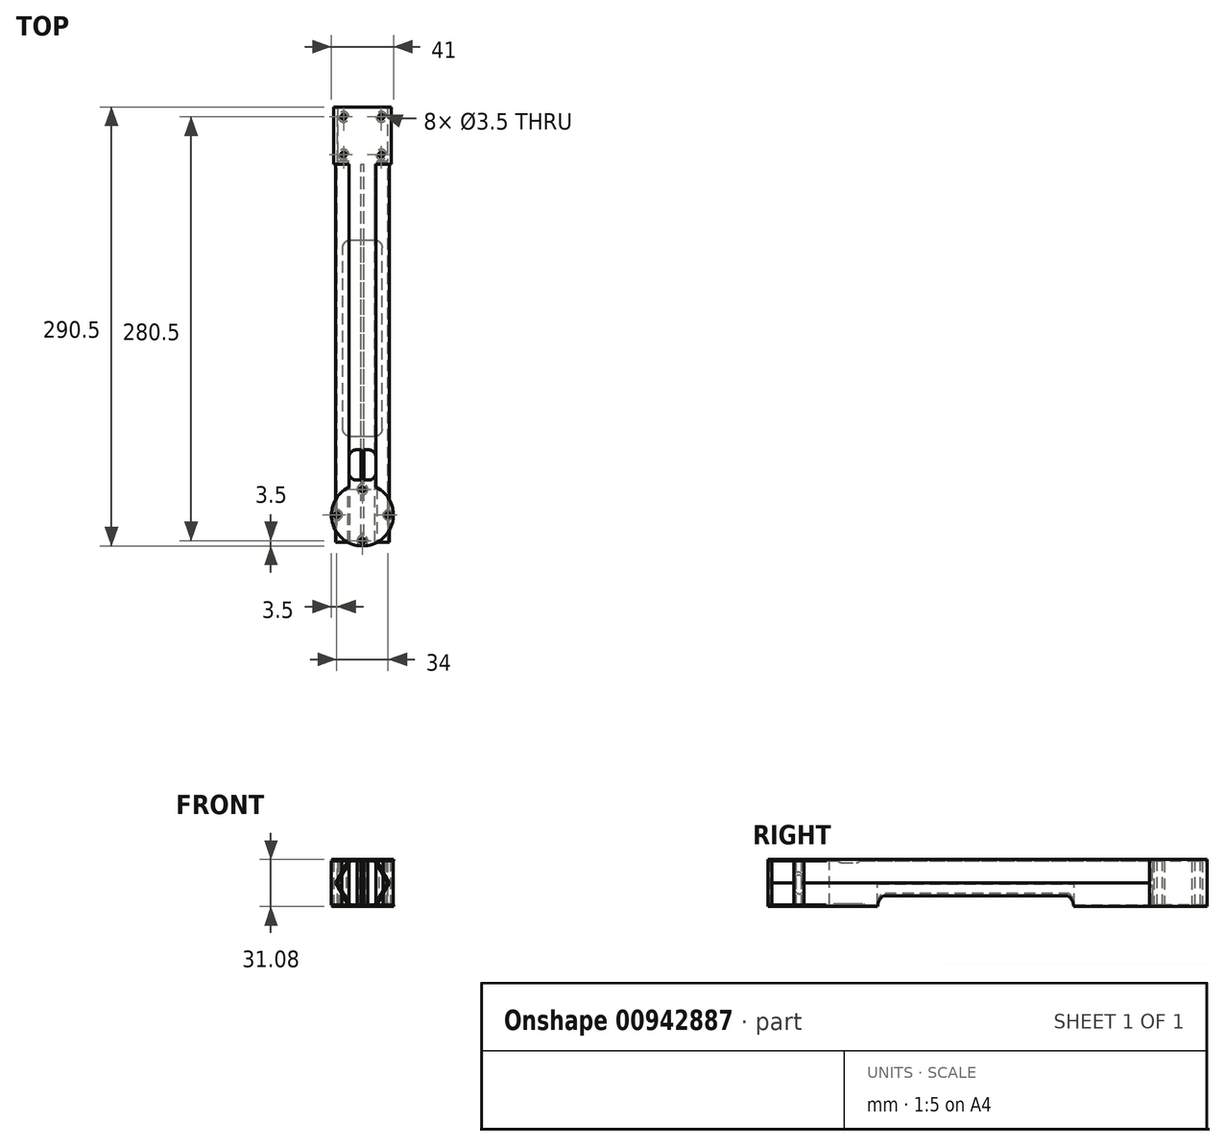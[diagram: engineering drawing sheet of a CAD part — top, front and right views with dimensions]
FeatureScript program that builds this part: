
annotation { "Feature Type Name" : "Feature", "Feature Type Description" : "" }
export const myFeature = defineFeature(function(context is Context, id is Id, definition is map)
    precondition{}
    {
        {
            var Q0;
            Q0=qCreatedBy(makeId("Front.planeOp"),FACE);
            var sketch = newSketch(context, id + "F0", { "sketchPlane" : qUnion([Q0])});
            skCircle(sketch, "E0.cCircle", {"center": v(0, 0) * mm, "radius": 14.5 * mm, "construction": true});
            skLineSegment(sketch, "E0.0", {"start": v(8.37, -14.5) * mm, "end": v(-8.37, -14.5) * mm});
            skLineSegment(sketch, "E0.1", {"start": v(-8.37, -14.5) * mm, "end": v(-16.74, 0) * mm});
            skLineSegment(sketch, "E0.2", {"start": v(-16.74, 0) * mm, "end": v(-8.37, 14.5) * mm});
            skLineSegment(sketch, "E0.3", {"start": v(-8.37, 14.5) * mm, "end": v(8.37, 14.5) * mm});
            skLineSegment(sketch, "E0.4", {"start": v(8.37, 14.5) * mm, "end": v(16.74, 0) * mm});
            skLineSegment(sketch, "E0.5", {"start": v(16.74, 0) * mm, "end": v(8.37, -14.5) * mm});
            skPoint(sketch, "E0.0.midPoint", {"position": v(0, -14.5) * mm});
            skCircle(sketch, "E1.cCircle", {"center": v(0, 0) * mm, "radius": 15.5 * mm, "construction": true});
            skLineSegment(sketch, "E1.0", {"start": v(8.95, -15.5) * mm, "end": v(-8.95, -15.5) * mm});
            skLineSegment(sketch, "E1.1", {"start": v(-8.95, -15.5) * mm, "end": v(-17.9, 0) * mm});
            skLineSegment(sketch, "E1.2", {"start": v(-17.9, 0) * mm, "end": v(-8.95, 15.5) * mm});
            skLineSegment(sketch, "E1.3", {"start": v(-8.95, 15.5) * mm, "end": v(8.95, 15.5) * mm});
            skLineSegment(sketch, "E1.4", {"start": v(8.95, 15.5) * mm, "end": v(17.9, 0) * mm});
            skLineSegment(sketch, "E1.5", {"start": v(17.9, 0) * mm, "end": v(8.95, -15.5) * mm});
            skPoint(sketch, "E1.0.midPoint", {"position": v(0, -15.5) * mm});
            skLineSegment(sketch, "E2", {"start": v(0, 14.5) * mm, "end": v(0, -14.5) * mm, "construction": true});
            skLineSegment(sketch, "E3.0", {"start": v(-1, 14.5) * mm, "end": v(-1, -14.5) * mm});
            skLineSegment(sketch, "E4.0", {"start": v(1, 14.5) * mm, "end": v(1, -14.5) * mm});
            skSolve(sketch);
        }
        {
            var Q0;
            Q0 = qSketchRegion(id + "F0", true);
            var Q1;
            {var subQ0=sQuery(id+"F0.wireOp",EDGE,"E3.0");Q1=makeQuery(id+"F0.imprint","IMPRINT",FACE,{"disambiguationData":[TD([[makeQuery(id+"F0.imprint","IMPRINT",EDGE,{"derivedFrom":subQ0}),1.0]])]});}
            extrude(context, id + "F1", {"entities" : qUnion([Q0, Q1]), "depth" : 250 * mm, "offsetDistance" : 25 * mm});
        }
        {
            var Q0;
            Q0=makeQuery(id+"F1.opExtrude","SWEPT_FACE",FACE,{"disambiguationData":[OSD([sQuery(id+"F0.wireOp",EDGE,"E1.3")])]});
            var sketch = newSketch(context, id + "F2", { "sketchPlane" : qUnion([Q0])});
            skLineSegment(sketch, "E5", {"start": v(0, -250) * mm, "end": v(0, -232) * mm, "construction": true});
            skCircle(sketch, "E6", {"center": v(0, -232) * mm, "radius": 20.5 * mm});
            skSolve(sketch);
        }
        {
            var Q0;
            {var subQ0=sQuery(id+"F2.wireOp",EDGE,"E6");var subQ1=makeQuery(id+"F1.opExtrude","SWEPT_EDGE",EDGE,{"disambiguationData":[OSD([sQuery(id+"F0.wireOp",EDGE,"E1.3"),sQuery(id+"F0.wireOp",EDGE,"E1.4")])]});var subQ2=makeQuery(id+"F2.imprint","INTERSECT",VERTEX,{"disambiguationData":[OD(0.0)],"derivedFrom":[subQ1,subQ0]});Q0=makeQuery(id+"F2.imprint","IMPRINT",FACE,{"disambiguationData":[TD([[makeQuery(id+"F2.imprint","IMPRINT",EDGE,{"disambiguationData":[TD([[subQ2,1.0]])],"derivedFrom":subQ0}),1.0]])]});}
            var Q1;
            {var subQ0=sQuery(id+"F2.wireOp",EDGE,"E6");var subQ1=sQuery(id+"F0.wireOp",EDGE,"E1.3");var subQ5=makeQuery(id+"F2.imprint","INTERSECT",VERTEX,{"derivedFrom":[makeQuery(id+"F1.opExtrude","CAP_EDGE",EDGE,{"disambiguationData":[OSD([subQ1])],"isStart":false}),subQ0]});Q1=makeQuery(id+"F2.imprint","IMPRINT",FACE,{"disambiguationData":[TD([[makeQuery(id+"F2.imprint","IMPRINT",EDGE,{"disambiguationData":[TD([[subQ5,1.0]])],"derivedFrom":subQ0}),1.0]])]});}
            var Q2;
            {var subQ0=sQuery(id+"F2.wireOp",EDGE,"E6");var subQ1=makeQuery(id+"F1.opExtrude","SWEPT_EDGE",EDGE,{"disambiguationData":[OSD([sQuery(id+"F0.wireOp",EDGE,"E1.2"),sQuery(id+"F0.wireOp",EDGE,"E1.3")])]});var subQ2=makeQuery(id+"F2.imprint","INTERSECT",VERTEX,{"disambiguationData":[OD(0.0)],"derivedFrom":[subQ1,subQ0]});Q2=makeQuery(id+"F2.imprint","IMPRINT",FACE,{"disambiguationData":[TD([[makeQuery(id+"F2.imprint","IMPRINT",EDGE,{"disambiguationData":[TD([[subQ2,-1.0]])],"derivedFrom":subQ0}),1.0]])]});}
            var Q3;
            {var subQ0=sQuery(id+"F0.wireOp",EDGE,"E0.3");Q3=makeQuery(id+"F1.opExtrude","SWEPT_FACE",FACE,{"disambiguationData":[OSD([subQ0]),TDD([makeQuery(id+"F0.imprint","IMPRINT",EDGE,{"disambiguationData":[TD([[makeQuery(id+"F0.imprint","INTERSECT",VERTEX,{"derivedFrom":[sQuery(id+"F0.wireOp",EDGE,"E0.2"),subQ0]}),-1.0]])],"derivedFrom":subQ0})])]});}
            extrude(context, id + "F3", {"entities" : qUnion([Q0, Q1, Q2]), "operationType" : NewBodyOperationType.ADD, "endBound" : BoundingType.UP_TO_SURFACE, "oppositeDirection" : true, "depth" : 25 * mm, "endBoundEntityFace" : qUnion([Q3]), "offsetDistance" : 25 * mm});
        }
        {
            var Q0;
            Q0=makeQuery(id+"F1.opExtrude","SWEPT_FACE",FACE,{"disambiguationData":[OSD([sQuery(id+"F0.wireOp",EDGE,"E1.0")])]});
            var sketch = newSketch(context, id + "F4", { "sketchPlane" : qUnion([Q0])});
            skArc(sketch, "E7.0", {"start": v(9.53, 213.85) * mm, "mid": v(0, 252.5) * mm, "end": v(-9.53, 213.85) * mm});
            skLineSegment(sketch, "E8", {"start": v(-9.53, 213.85) * mm, "end": v(9.53, 213.85) * mm});
            skSolve(sketch);
        }
        {
            var Q0;
            Q0 = qSketchRegion(id + "F4", true);
            var Q1;
            {var subQ0=sQuery(id+"F0.wireOp",EDGE,"E0.0");Q1=makeQuery(id+"F1.opExtrude","SWEPT_FACE",FACE,{"disambiguationData":[OSD([subQ0]),TDD([makeQuery(id+"F0.imprint","IMPRINT",EDGE,{"disambiguationData":[TD([[makeQuery(id+"F0.imprint","INTERSECT",VERTEX,{"derivedFrom":[subQ0,sQuery(id+"F0.wireOp",EDGE,"E0.1")]}),1.0]])],"derivedFrom":subQ0})])]});}
            extrude(context, id + "F5", {"entities" : qUnion([Q0]), "operationType" : NewBodyOperationType.ADD, "endBound" : BoundingType.UP_TO_SURFACE, "oppositeDirection" : true, "depth" : 25 * mm, "endBoundEntityFace" : qUnion([Q1]), "offsetDistance" : 25 * mm});
        }
        {
            var Q0;
            {var subQ0=sQuery(id+"F0.wireOp",EDGE,"E0.1");var subQ1=sQuery(id+"F0.wireOp",EDGE,"E0.0");var subQ2=sQuery(id+"F0.wireOp",EDGE,"E3.0");var subQ3=sQuery(id+"F0.wireOp",EDGE,"E0.2");var subQ4=sQuery(id+"F0.wireOp",EDGE,"E0.5");var subQ5=sQuery(id+"F0.wireOp",EDGE,"E4.0");var subQ6=sQuery(id+"F0.wireOp",EDGE,"E1.1");var subQ7=sQuery(id+"F0.wireOp",EDGE,"E0.3");var subQ8=sQuery(id+"F0.wireOp",EDGE,"E0.4");var subQ9=sQuery(id+"F0.wireOp",EDGE,"E1.2");Q0=makeQuery(id+"F5.boolean.opBoolean","SPLIT",FACE,{"disambiguationData":[TD([makeQuery(id+"F1.opExtrude","SWEPT_FACE",FACE,{"disambiguationData":[OSD([subQ0])]})])],"derivedFrom":makeQuery(id+"F1.opExtrude","CAP_FACE",FACE,{"disambiguationData":[OSD([subQ1,subQ0,subQ3,subQ7,subQ8,subQ4,sQuery(id+"F0.wireOp",EDGE,"E1.0"),subQ6,subQ9,sQuery(id+"F0.wireOp",EDGE,"E1.3"),sQuery(id+"F0.wireOp",EDGE,"E1.4"),sQuery(id+"F0.wireOp",EDGE,"E1.5"),subQ2,subQ5])],"isStart":false})});}
            var sketch = newSketch(context, id + "F6", { "sketchPlane" : qUnion([Q0])});
            skLineSegment(sketch, "E9.0", {"start": v(-9.53, -14.5) * mm, "end": v(-17.9, 0) * mm});
            skLineSegment(sketch, "E10.0", {"start": v(-17.9, 0) * mm, "end": v(-9.53, 14.5) * mm});
            skLineSegment(sketch, "E11.0", {"start": v(-16.74, 0) * mm, "end": v(-8.37, 14.5) * mm});
            skLineSegment(sketch, "E12.0", {"start": v(-8.37, -14.5) * mm, "end": v(-16.74, 0) * mm});
            skLineSegment(sketch, "E13.0", {"start": v(16.74, 0) * mm, "end": v(8.37, -14.5) * mm});
            skLineSegment(sketch, "E14.0", {"start": v(17.9, 0) * mm, "end": v(9.53, -14.5) * mm});
            skLineSegment(sketch, "E15.0", {"start": v(9.53, 14.5) * mm, "end": v(17.9, 0) * mm});
            skLineSegment(sketch, "E16.0", {"start": v(8.37, 14.5) * mm, "end": v(16.74, 0) * mm});
            skLineSegment(sketch, "E17.0", {"start": v(1, 14.5) * mm, "end": v(1, -14.5) * mm});
            skLineSegment(sketch, "E18.0", {"start": v(-1, 14.5) * mm, "end": v(-1, -14.5) * mm});
            skLineSegment(sketch, "E19", {"start": v(-9.53, 14.5) * mm, "end": v(-8.37, 14.5) * mm});
            skLineSegment(sketch, "E20", {"start": v(-1, 14.5) * mm, "end": v(1, 14.5) * mm});
            skLineSegment(sketch, "E21", {"start": v(8.37, 14.5) * mm, "end": v(9.53, 14.5) * mm});
            skLineSegment(sketch, "E22", {"start": v(8.37, -14.5) * mm, "end": v(9.53, -14.5) * mm});
            skLineSegment(sketch, "E23", {"start": v(-1, -14.5) * mm, "end": v(1, -14.5) * mm});
            skLineSegment(sketch, "E24", {"start": v(-9.53, -14.5) * mm, "end": v(-8.37, -14.5) * mm});
            skSolve(sketch);
        }
        {
            var Q0;
            Q0=makeQuery(id+"F6.imprint","IMPRINT",FACE,{"disambiguationData":[TD([[makeQuery(id+"F6.imprint","IMPRINT",EDGE,{"derivedFrom":sQuery(id+"F6.wireOp",EDGE,"E17.0")}),-1.0]])]});
            var Q1;
            Q1=makeQuery(id+"F3.opExtrude","SWEPT_FACE",FACE,{"disambiguationData":[OSD([sQuery(id+"F2.wireOp",EDGE,"E6")])]});
            extrude(context, id + "F7", {"entities" : qUnion([Q0]), "operationType" : NewBodyOperationType.ADD, "endBound" : BoundingType.UP_TO_SURFACE, "depth" : 25 * mm, "endBoundEntityFace" : qUnion([Q1]), "offsetDistance" : 25 * mm});
        }
        {
            var Q0;
            Q0=makeQuery(id+"F3.boolean.opBoolean","MERGE",FACE,{"derivedFrom":[makeQuery(id+"F1.opExtrude","SWEPT_FACE",FACE,{"disambiguationData":[OSD([sQuery(id+"F0.wireOp",EDGE,"E1.3")])]}),makeQuery(id+"F3.opExtrude","CAP_FACE",FACE,{"disambiguationData":[OSD([sQuery(id+"F2.wireOp",EDGE,"E6")])],"isStart":true})]});
            var sketch = newSketch(context, id + "F8", { "sketchPlane" : qUnion([Q0])});
            skCircle(sketch, "E25", {"center": v(0, -232) * mm, "radius": 17 * mm, "construction": true});
            skLineSegment(sketch, "E26", {"start": v(0, -232) * mm, "end": v(17, -232) * mm, "construction": true});
            skLineSegment(sketch, "E27", {"start": v(0, -232) * mm, "end": v(-17, -232) * mm, "construction": true});
            skLineSegment(sketch, "E28", {"start": v(0, -232) * mm, "end": v(0, -215) * mm, "construction": true});
            skLineSegment(sketch, "E29", {"start": v(0, -232) * mm, "end": v(0, -249) * mm, "construction": true});
            skCircle(sketch, "E30", {"center": v(0, -215) * mm, "radius": 1.75 * mm});
            skCircle(sketch, "E31", {"center": v(-17, -232) * mm, "radius": 1.75 * mm});
            skCircle(sketch, "E32", {"center": v(0, -249) * mm, "radius": 1.75 * mm});
            skCircle(sketch, "E33", {"center": v(17, -232) * mm, "radius": 1.75 * mm});
            skSolve(sketch);
        }
        {
            var Q0;
            Q0 = qSketchRegion(id + "F8", true);
            var Q1;
            Q1=makeQuery(id+"F5.boolean.opBoolean","MERGE",FACE,{"derivedFrom":[makeQuery(id+"F1.opExtrude","SWEPT_FACE",FACE,{"disambiguationData":[OSD([sQuery(id+"F0.wireOp",EDGE,"E1.0")])]}),makeQuery(id+"F5.opExtrude","CAP_FACE",FACE,{"disambiguationData":[OSD([sQuery(id+"F4.wireOp",EDGE,"E7.0"),sQuery(id+"F4.wireOp",EDGE,"E8")])],"isStart":true})]});
            extrude(context, id + "F9", {"entities" : qUnion([Q0]), "operationType" : NewBodyOperationType.REMOVE, "endBound" : BoundingType.UP_TO_SURFACE, "oppositeDirection" : true, "depth" : 25 * mm, "endBoundEntityFace" : qUnion([Q1]), "offsetDistance" : 25 * mm});
        }
        {
            var Q0;
            Q0=makeQuery(id+"F3.boolean.opBoolean","MERGE",FACE,{"derivedFrom":[makeQuery(id+"F1.opExtrude","SWEPT_FACE",FACE,{"disambiguationData":[OSD([sQuery(id+"F0.wireOp",EDGE,"E1.3")])]}),makeQuery(id+"F3.opExtrude","CAP_FACE",FACE,{"disambiguationData":[OSD([sQuery(id+"F2.wireOp",EDGE,"E6")])],"isStart":true})]});
            var sketch = newSketch(context, id + "F10", { "sketchPlane" : qUnion([Q0])});
            skLineSegment(sketch, "E34.0.0", {"start": v(-8.95, 0) * mm, "end": v(-8.95, -213.56) * mm});
            skArc(sketch, "E34.0.1", {"start": v(-8.95, -213.56) * mm, "mid": v(0, -252.5) * mm, "end": v(8.95, -213.56) * mm});
            skLineSegment(sketch, "E34.0.2", {"start": v(8.95, -213.56) * mm, "end": v(8.95, 0) * mm});
            skLineSegment(sketch, "E34.0.3", {"start": v(8.95, 0) * mm, "end": v(-8.95, 0) * mm});
            skPoint(sketch, "E35.0", {"position": v(-1, -213.56) * mm});
            skCircle(sketch, "E36.0", {"center": v(17, -232) * mm, "radius": 1.75 * mm});
            skCircle(sketch, "E37.0", {"center": v(0, -249) * mm, "radius": 1.75 * mm});
            skCircle(sketch, "E38.0", {"center": v(0, -215) * mm, "radius": 1.75 * mm});
            skCircle(sketch, "E39", {"center": v(-17, -232) * mm, "radius": 3.5 * mm});
            skCircle(sketch, "E40", {"center": v(0, -215) * mm, "radius": 3.5 * mm});
            skCircle(sketch, "E41", {"center": v(17, -232) * mm, "radius": 3.25 * mm});
            skCircle(sketch, "E42", {"center": v(0, -249) * mm, "radius": 3.5 * mm});
            skSolve(sketch);
        }
        {
            var Q0;
            Q0=makeQuery(id+"F10.imprint","IMPRINT",FACE,{"disambiguationData":[TD([[makeQuery(id+"F10.imprint","IMPRINT",EDGE,{"derivedFrom":sQuery(id+"F10.wireOp",EDGE,"E39")}),1.0]])]});
            var Q1;
            Q1=makeQuery(id+"F10.imprint","IMPRINT",FACE,{"disambiguationData":[TD([[makeQuery(id+"F10.imprint","IMPRINT",EDGE,{"derivedFrom":sQuery(id+"F10.wireOp",EDGE,"E38.0")}),-1.0]])]});
            var Q2;
            Q2=makeQuery(id+"F10.imprint","IMPRINT",FACE,{"disambiguationData":[TD([[makeQuery(id+"F10.imprint","IMPRINT",EDGE,{"derivedFrom":sQuery(id+"F10.wireOp",EDGE,"E37.0")}),-1.0]])]});
            var Q3;
            Q3=makeQuery(id+"F10.imprint","IMPRINT",FACE,{"disambiguationData":[TD([[makeQuery(id+"F10.imprint","IMPRINT",EDGE,{"derivedFrom":sQuery(id+"F10.wireOp",EDGE,"E36.0")}),-1.0]])]});
            var Q4;
            Q4=makeQuery(id+"F5.boolean.opBoolean","MERGE",FACE,{"derivedFrom":[makeQuery(id+"F1.opExtrude","SWEPT_FACE",FACE,{"disambiguationData":[OSD([sQuery(id+"F0.wireOp",EDGE,"E1.0")])]}),makeQuery(id+"F5.opExtrude","CAP_FACE",FACE,{"disambiguationData":[OSD([sQuery(id+"F4.wireOp",EDGE,"E7.0"),sQuery(id+"F4.wireOp",EDGE,"E8")])],"isStart":true})]});
            extrude(context, id + "F11", {"entities" : qUnion([Q0, Q1, Q2, Q3]), "operationType" : NewBodyOperationType.ADD, "endBound" : BoundingType.UP_TO_SURFACE, "oppositeDirection" : true, "depth" : 25 * mm, "endBoundEntityFace" : qUnion([Q4]), "offsetDistance" : 25 * mm});
        }
        {
            var Q0;
            Q0=makeQuery(id+"F3.boolean.opBoolean","MERGE",FACE,{"derivedFrom":[makeQuery(id+"F1.opExtrude","SWEPT_FACE",FACE,{"disambiguationData":[OSD([sQuery(id+"F0.wireOp",EDGE,"E1.3")])]}),makeQuery(id+"F3.opExtrude","CAP_FACE",FACE,{"disambiguationData":[OSD([sQuery(id+"F2.wireOp",EDGE,"E6")])],"isStart":true})]});
            var sketch = newSketch(context, id + "F12", { "sketchPlane" : qUnion([Q0])});
            skLineSegment(sketch, "E43.bottom", {"start": v(-19, 38) * mm, "end": v(19, 38) * mm});
            skLineSegment(sketch, "E43.top", {"start": v(-19, 0) * mm, "end": v(19, 0) * mm});
            skLineSegment(sketch, "E43.left", {"start": v(-19, 38) * mm, "end": v(-19, 0) * mm});
            skLineSegment(sketch, "E43.right", {"start": v(19, 38) * mm, "end": v(19, 0) * mm});
            skPoint(sketch, "E44", {"position": v(0, 0) * mm});
            skSolve(sketch);
        }
        {
            var Q0;
            Q0=makeQuery(id+"F12.imprint","IMPRINT",FACE,{"disambiguationData":[TD([[makeQuery(id+"F12.imprint","IMPRINT",EDGE,{"derivedFrom":sQuery(id+"F12.wireOp",EDGE,"E43.bottom")}),-1.0]])]});
            var Q1;
            {var subQ0=sQuery(id+"F0.wireOp",EDGE,"E0.2");var subQ10=sQuery(id+"F0.wireOp",EDGE,"E0.4");var subQ11=sQuery(id+"F0.wireOp",EDGE,"E0.3");var subQ14=sQuery(id+"F2.wireOp",EDGE,"E6");Q1=makeQuery(id+"F7.boolean.opBoolean","SPLIT",FACE,{"disambiguationData":[TD([makeQuery(id+"F1.opExtrude","SWEPT_FACE",FACE,{"disambiguationData":[OSD([subQ0])]})])],"derivedFrom":makeQuery(id+"F3.boolean.opBoolean","MERGE",FACE,{"derivedFrom":[makeQuery(id+"F1.opExtrude","SWEPT_FACE",FACE,{"disambiguationData":[OSD([subQ11]),TDD([makeQuery(id+"F0.imprint","IMPRINT",EDGE,{"disambiguationData":[TD([[makeQuery(id+"F0.imprint","INTERSECT",VERTEX,{"derivedFrom":[subQ0,subQ11]}),-1.0]])],"derivedFrom":subQ11})])]}),makeQuery(id+"F1.opExtrude","SWEPT_FACE",FACE,{"disambiguationData":[OSD([subQ11]),TDD([makeQuery(id+"F0.imprint","IMPRINT",EDGE,{"disambiguationData":[TD([[makeQuery(id+"F0.imprint","INTERSECT",VERTEX,{"derivedFrom":[subQ11,subQ10]}),1.0]])],"derivedFrom":subQ11})])]}),makeQuery(id+"F3.opExtrude","CAP_FACE",FACE,{"disambiguationData":[OSD([subQ14])],"isStart":false})]})});}
            extrude(context, id + "F13", {"entities" : qUnion([Q0]), "operationType" : NewBodyOperationType.ADD, "endBound" : BoundingType.UP_TO_SURFACE, "oppositeDirection" : true, "depth" : 25 * mm, "endBoundEntityFace" : qUnion([Q1]), "offsetDistance" : 25 * mm});
        }
        {
            var Q0;
            Q0=makeQuery(id+"F5.boolean.opBoolean","MERGE",FACE,{"derivedFrom":[makeQuery(id+"F1.opExtrude","SWEPT_FACE",FACE,{"disambiguationData":[OSD([sQuery(id+"F0.wireOp",EDGE,"E1.0")])]}),makeQuery(id+"F5.opExtrude","CAP_FACE",FACE,{"disambiguationData":[OSD([sQuery(id+"F4.wireOp",EDGE,"E7.0"),sQuery(id+"F4.wireOp",EDGE,"E8")])],"isStart":true})]});
            var sketch = newSketch(context, id + "F14", { "sketchPlane" : qUnion([Q0])});
            skLineSegment(sketch, "E45.0", {"start": v(19, -38) * mm, "end": v(-19, -38) * mm});
            skLineSegment(sketch, "E46.0", {"start": v(19, 0) * mm, "end": v(19, -38) * mm});
            skLineSegment(sketch, "E47.0", {"start": v(-19, 0) * mm, "end": v(-19, -38) * mm});
            skLineSegment(sketch, "E48", {"start": v(19, 0) * mm, "end": v(-19, 0) * mm});
            skSolve(sketch);
        }
        {
            var Q0;
            Q0 = qSketchRegion(id + "F14", true);
            var Q1;
            {var subQ0=sQuery(id+"F0.wireOp",EDGE,"E0.1");var subQ9=sQuery(id+"F0.wireOp",EDGE,"E0.5");var subQ13=sQuery(id+"F0.wireOp",EDGE,"E0.0");var subQ15=sQuery(id+"F4.wireOp",EDGE,"E7.0");var subQ16=sQuery(id+"F4.wireOp",EDGE,"E8");Q1=makeQuery(id+"F7.boolean.opBoolean","SPLIT",FACE,{"disambiguationData":[TD([makeQuery(id+"F1.opExtrude","SWEPT_FACE",FACE,{"disambiguationData":[OSD([subQ0])]})])],"derivedFrom":makeQuery(id+"F5.boolean.opBoolean","MERGE",FACE,{"derivedFrom":[makeQuery(id+"F1.opExtrude","SWEPT_FACE",FACE,{"disambiguationData":[OSD([subQ13]),TDD([makeQuery(id+"F0.imprint","IMPRINT",EDGE,{"disambiguationData":[TD([[makeQuery(id+"F0.imprint","INTERSECT",VERTEX,{"derivedFrom":[subQ13,subQ9]}),-1.0]])],"derivedFrom":subQ13})])]}),makeQuery(id+"F1.opExtrude","SWEPT_FACE",FACE,{"disambiguationData":[OSD([subQ13]),TDD([makeQuery(id+"F0.imprint","IMPRINT",EDGE,{"disambiguationData":[TD([[makeQuery(id+"F0.imprint","INTERSECT",VERTEX,{"derivedFrom":[subQ13,subQ0]}),1.0]])],"derivedFrom":subQ13})])]}),makeQuery(id+"F5.opExtrude","CAP_FACE",FACE,{"disambiguationData":[OSD([subQ15,subQ16])],"isStart":false})]})});}
            extrude(context, id + "F15", {"entities" : qUnion([Q0]), "operationType" : NewBodyOperationType.ADD, "endBound" : BoundingType.UP_TO_SURFACE, "oppositeDirection" : true, "depth" : 25 * mm, "endBoundEntityFace" : qUnion([Q1]), "offsetDistance" : 25 * mm});
        }
        {
            var Q0;
            Q0=makeQuery(id+"F13.opExtrude","SWEPT_FACE",FACE,{"disambiguationData":[OSD([sQuery(id+"F12.wireOp",EDGE,"E43.left")])]});
            var sketch = newSketch(context, id + "F16", { "sketchPlane" : qUnion([Q0])});
            skLineSegment(sketch, "E49.bottom", {"start": v(-38, 15.5) * mm, "end": v(0, 15.5) * mm});
            skLineSegment(sketch, "E49.top", {"start": v(-38, -15.58) * mm, "end": v(0, -15.58) * mm});
            skLineSegment(sketch, "E49.left", {"start": v(-38, 15.5) * mm, "end": v(-38, -15.58) * mm});
            skLineSegment(sketch, "E49.right", {"start": v(0, 15.5) * mm, "end": v(0, -15.58) * mm});
            skSolve(sketch);
        }
        {
            var Q0;
            {var subQ0=sQuery(id+"F16.wireOp",EDGE,"E49.top");Q0=makeQuery(id+"F16.imprint","IMPRINT",FACE,{"disambiguationData":[TD([[makeQuery(id+"F16.imprint","IMPRINT",EDGE,{"derivedFrom":subQ0}),1.0]])]});}
            extrude(context, id + "F17", {"entities" : qUnion([Q0]), "operationType" : NewBodyOperationType.ADD, "oppositeDirection" : true, "depth" : 2.4 * mm, "offsetDistance" : 25 * mm});
        }
        {
            var Q0;
            Q0=makeQuery(id+"F13.opExtrude","SWEPT_FACE",FACE,{"disambiguationData":[OSD([sQuery(id+"F12.wireOp",EDGE,"E43.right")])]});
            var sketch = newSketch(context, id + "F18", { "sketchPlane" : qUnion([Q0])});
            skLineSegment(sketch, "E50.bottom", {"start": v(38, 15.5) * mm, "end": v(0, 15.5) * mm});
            skLineSegment(sketch, "E50.top", {"start": v(38, -15.48) * mm, "end": v(0, -15.48) * mm});
            skLineSegment(sketch, "E50.left", {"start": v(38, 15.5) * mm, "end": v(38, -15.48) * mm});
            skLineSegment(sketch, "E50.right", {"start": v(0, 15.5) * mm, "end": v(0, -15.48) * mm});
            skSolve(sketch);
        }
        {
            var Q0;
            Q0 = qSketchRegion(id + "F18", true);
            extrude(context, id + "F19", {"entities" : qUnion([Q0]), "operationType" : NewBodyOperationType.ADD, "oppositeDirection" : true, "depth" : 2.4 * mm, "offsetDistance" : 25 * mm});
        }
        {
            var Q0;
            {var subQ3=sQuery(id+"F14.wireOp",EDGE,"E48");var subQ9=sQuery(id+"F0.wireOp",EDGE,"E1.2");var subQ10=sQuery(id+"F0.wireOp",EDGE,"E1.1");var subQ22=sQuery(id+"F12.wireOp",EDGE,"E43.top");Q0=makeQuery(id+"F17.boolean.opBoolean","MERGE",FACE,{"derivedFrom":[makeQuery(id+"F13.boolean.opBoolean","SPLIT",FACE,{"disambiguationData":[TD([makeQuery(id+"F1.opExtrude","SWEPT_FACE",FACE,{"disambiguationData":[OSD([subQ9])]})])],"derivedFrom":makeQuery(id+"F13.opExtrude","SWEPT_FACE",FACE,{"disambiguationData":[OSD([subQ22])]})}),makeQuery(id+"F15.boolean.opBoolean","SPLIT",FACE,{"disambiguationData":[TD([makeQuery(id+"F1.opExtrude","SWEPT_FACE",FACE,{"disambiguationData":[OSD([subQ10])]})])],"derivedFrom":makeQuery(id+"F15.opExtrude","SWEPT_FACE",FACE,{"disambiguationData":[OSD([subQ3])]})}),makeQuery(id+"F17.opExtrude","SWEPT_FACE",FACE,{"disambiguationData":[OSD([sQuery(id+"F16.wireOp",EDGE,"E49.right")])]})]});}
            var sketch = newSketch(context, id + "F20", { "sketchPlane" : qUnion([Q0])});
            skLineSegment(sketch, "E51", {"start": v(-19, -15.58) * mm, "end": v(-8.95, -15.5) * mm});
            skLineSegment(sketch, "E52", {"start": v(-8.95, -15.5) * mm, "end": v(-19, 2.25) * mm});
            skLineSegment(sketch, "E53", {"start": v(-19, 2.25) * mm, "end": v(-19, -15.58) * mm});
            skLineSegment(sketch, "E54", {"start": v(-8.95, 15.5) * mm, "end": v(-19, -2.25) * mm});
            skLineSegment(sketch, "E55", {"start": v(-19, -2.25) * mm, "end": v(-19, 15.5) * mm});
            skLineSegment(sketch, "E56", {"start": v(-19, 15.5) * mm, "end": v(-8.95, 15.5) * mm});
            skLineSegment(sketch, "E57", {"start": v(18.71, -15.5) * mm, "end": v(8.93, -15.5) * mm});
            skPoint(sketch, "E57.startSnap0", {"position": v(-12.77, -15.5) * mm});
            skPoint(sketch, "E57.endSnap0", {"position": v(-12.77, -15.5) * mm});
            skLineSegment(sketch, "E58", {"start": v(8.93, -15.5) * mm, "end": v(18.48, 2.25) * mm});
            skLineSegment(sketch, "E59", {"start": v(18.48, 2.25) * mm, "end": v(18.71, -15.5) * mm});
            skLineSegment(sketch, "E60", {"start": v(8.93, 15.5) * mm, "end": v(18.48, -1.37) * mm});
            skLineSegment(sketch, "E61", {"start": v(18.48, -1.37) * mm, "end": v(18.48, 15.5) * mm});
            skLineSegment(sketch, "E62", {"start": v(18.48, 15.5) * mm, "end": v(8.93, 15.5) * mm});
            skSolve(sketch);
        }
        {
            var Q0;
            Q0 = qSketchRegion(id + "F20", true);
            extrude(context, id + "F21", {"entities" : qUnion([Q0]), "operationType" : NewBodyOperationType.ADD, "oppositeDirection" : true, "depth" : 2 * mm, "offsetDistance" : 25 * mm});
        }
        {
            var Q0;
            Q0=makeQuery(id+"F15.boolean.opBoolean","MERGE",FACE,{"derivedFrom":[makeQuery(id+"F5.boolean.opBoolean","MERGE",FACE,{"derivedFrom":[makeQuery(id+"F1.opExtrude","SWEPT_FACE",FACE,{"disambiguationData":[OSD([sQuery(id+"F0.wireOp",EDGE,"E1.0")])]}),makeQuery(id+"F5.opExtrude","CAP_FACE",FACE,{"disambiguationData":[OSD([sQuery(id+"F4.wireOp",EDGE,"E7.0"),sQuery(id+"F4.wireOp",EDGE,"E8")])],"isStart":true})]}),makeQuery(id+"F15.opExtrude","CAP_FACE",FACE,{"disambiguationData":[OSD([sQuery(id+"F14.wireOp",EDGE,"E45.0"),sQuery(id+"F14.wireOp",EDGE,"E46.0"),sQuery(id+"F14.wireOp",EDGE,"E47.0"),sQuery(id+"F14.wireOp",EDGE,"E48")])],"isStart":true})]});
            var sketch = newSketch(context, id + "F22", { "sketchPlane" : qUnion([Q0])});
            skLineSegment(sketch, "E63", {"start": v(0, -38) * mm, "end": v(0, 213.25) * mm, "construction": true});
            skLineSegment(sketch, "E64.bottom", {"start": v(-13, 180) * mm, "end": v(13, 180) * mm});
            skLineSegment(sketch, "E64.top", {"start": v(-13, 50) * mm, "end": v(13, 50) * mm});
            skLineSegment(sketch, "E64.left", {"start": v(-13, 180) * mm, "end": v(-13, 50) * mm});
            skLineSegment(sketch, "E64.right", {"start": v(13, 180) * mm, "end": v(13, 50) * mm});
            skPoint(sketch, "E65", {"position": v(0, 180) * mm});
            skSolve(sketch);
        }
        {
            var Q0;
            Q0 = qSketchRegion(id + "F22", true);
            extrude(context, id + "F23", {"entities" : qUnion([Q0]), "operationType" : NewBodyOperationType.REMOVE, "oppositeDirection" : true, "depth" : 15 * mm, "offsetDistance" : 25 * mm});
        }
        {
            var Q0;
            {var subQ0=sQuery(id+"F4.wireOp",EDGE,"E8");var subQ1=sQuery(id+"F4.wireOp",EDGE,"E7.0");var subQ2=makeQuery(id+"F5.opExtrude","CAP_FACE",FACE,{"disambiguationData":[OSD([subQ1,subQ0])],"isStart":true});var subQ7=makeQuery(id+"F1.opExtrude","SWEPT_FACE",FACE,{"disambiguationData":[OSD([sQuery(id+"F0.wireOp",EDGE,"E1.0")])]});var subQ17=sQuery(id+"F2.wireOp",EDGE,"E6");Q0=makeQuery(id+"F23.boolean.opBoolean","SPLIT",FACE,{"disambiguationData":[TD([makeQuery(id+"F3.opExtrude","SWEPT_FACE",FACE,{"disambiguationData":[OSD([subQ17])]})])],"derivedFrom":makeQuery(id+"F15.boolean.opBoolean","MERGE",FACE,{"derivedFrom":[makeQuery(id+"F5.boolean.opBoolean","MERGE",FACE,{"derivedFrom":[subQ7,subQ2]}),makeQuery(id+"F15.opExtrude","CAP_FACE",FACE,{"disambiguationData":[OSD([sQuery(id+"F14.wireOp",EDGE,"E45.0"),sQuery(id+"F14.wireOp",EDGE,"E46.0"),sQuery(id+"F14.wireOp",EDGE,"E47.0"),sQuery(id+"F14.wireOp",EDGE,"E48")])],"isStart":true})]})});}
            var sketch = newSketch(context, id + "F24", { "sketchPlane" : qUnion([Q0])});
            skLineSegment(sketch, "E66.bottom", {"start": v(8.95, 188.85) * mm, "end": v(-8.95, 188.85) * mm});
            skLineSegment(sketch, "E66.top", {"start": v(8.95, 208.85) * mm, "end": v(-8.95, 208.85) * mm});
            skLineSegment(sketch, "E66.left", {"start": v(8.95, 188.85) * mm, "end": v(8.95, 208.85) * mm});
            skLineSegment(sketch, "E66.right", {"start": v(-8.95, 188.85) * mm, "end": v(-8.95, 208.85) * mm});
            skSolve(sketch);
        }
        {
            var Q0;
            Q0 = qSketchRegion(id + "F24", true);
            extrude(context, id + "F25", {"entities" : qUnion([Q0]), "operationType" : NewBodyOperationType.REMOVE, "oppositeDirection" : true, "depth" : 2 * mm, "offsetDistance" : 25 * mm});
        }
        {
            var Q0;
            Q0=makeQuery(id+"F13.boolean.opBoolean","MERGE",FACE,{"derivedFrom":[makeQuery(id+"F3.boolean.opBoolean","MERGE",FACE,{"derivedFrom":[makeQuery(id+"F1.opExtrude","SWEPT_FACE",FACE,{"disambiguationData":[OSD([sQuery(id+"F0.wireOp",EDGE,"E1.3")])]}),makeQuery(id+"F3.opExtrude","CAP_FACE",FACE,{"disambiguationData":[OSD([sQuery(id+"F2.wireOp",EDGE,"E6")])],"isStart":true})]}),makeQuery(id+"F13.opExtrude","CAP_FACE",FACE,{"disambiguationData":[OSD([sQuery(id+"F12.wireOp",EDGE,"E43.bottom"),sQuery(id+"F12.wireOp",EDGE,"E43.top"),sQuery(id+"F12.wireOp",EDGE,"E43.left"),sQuery(id+"F12.wireOp",EDGE,"E43.right")])],"isStart":true})]});
            var sketch = newSketch(context, id + "F26", { "sketchPlane" : qUnion([Q0])});
            skLineSegment(sketch, "E67.0", {"start": v(8.95, -208.85) * mm, "end": v(-8.95, -208.85) * mm});
            skLineSegment(sketch, "E68.0", {"start": v(8.95, -188.85) * mm, "end": v(-8.95, -188.85) * mm});
            skLineSegment(sketch, "E69.0", {"start": v(-8.95, -208.85) * mm, "end": v(-8.95, -188.85) * mm});
            skLineSegment(sketch, "E70.0", {"start": v(8.95, -208.85) * mm, "end": v(8.95, -188.85) * mm});
            skSolve(sketch);
        }
        {
            var Q0;
            Q0 = qSketchRegion(id + "F26", true);
            extrude(context, id + "F27", {"entities" : qUnion([Q0]), "operationType" : NewBodyOperationType.REMOVE, "oppositeDirection" : true, "depth" : 2 * mm, "offsetDistance" : 25 * mm});
        }
        {
            var Q0;
            Q0=makeQuery(id+"F27.boolean.opBoolean","COPY",EDGE,{"derivedFrom":makeQuery(id+"F27.opExtrude","SWEPT_EDGE",EDGE,{"disambiguationData":[OSD([sQuery(id+"F0.wireOp",EDGE,"E1.2"),sQuery(id+"F0.wireOp",EDGE,"E1.3"),sQuery(id+"F26.wireOp",EDGE,"E67.0"),sQuery(id+"F26.wireOp",EDGE,"E69.0")])]})});
            var Q1;
            Q1=makeQuery(id+"F27.boolean.opBoolean","COPY",EDGE,{"derivedFrom":makeQuery(id+"F27.opExtrude","SWEPT_EDGE",EDGE,{"disambiguationData":[OSD([sQuery(id+"F0.wireOp",EDGE,"E1.3"),sQuery(id+"F0.wireOp",EDGE,"E1.4"),sQuery(id+"F26.wireOp",EDGE,"E67.0"),sQuery(id+"F26.wireOp",EDGE,"E70.0")])]})});
            var Q2;
            Q2=makeQuery(id+"F27.boolean.opBoolean","COPY",EDGE,{"derivedFrom":makeQuery(id+"F27.opExtrude","SWEPT_EDGE",EDGE,{"disambiguationData":[OSD([sQuery(id+"F0.wireOp",EDGE,"E1.2"),sQuery(id+"F0.wireOp",EDGE,"E1.3"),sQuery(id+"F26.wireOp",EDGE,"E68.0"),sQuery(id+"F26.wireOp",EDGE,"E69.0")])]})});
            var Q3;
            Q3=makeQuery(id+"F27.boolean.opBoolean","COPY",EDGE,{"derivedFrom":makeQuery(id+"F27.opExtrude","SWEPT_EDGE",EDGE,{"disambiguationData":[OSD([sQuery(id+"F0.wireOp",EDGE,"E1.3"),sQuery(id+"F0.wireOp",EDGE,"E1.4"),sQuery(id+"F26.wireOp",EDGE,"E68.0"),sQuery(id+"F26.wireOp",EDGE,"E70.0")])]})});
            var Q4;
            Q4=makeQuery(id+"F25.boolean.opBoolean","COPY",EDGE,{"derivedFrom":makeQuery(id+"F25.opExtrude","SWEPT_EDGE",EDGE,{"disambiguationData":[OSD([sQuery(id+"F0.wireOp",EDGE,"E1.0"),sQuery(id+"F0.wireOp",EDGE,"E1.1"),sQuery(id+"F24.wireOp",EDGE,"E66.bottom"),sQuery(id+"F24.wireOp",EDGE,"E66.right")])]})});
            var Q5;
            Q5=makeQuery(id+"F25.boolean.opBoolean","COPY",EDGE,{"derivedFrom":makeQuery(id+"F25.opExtrude","SWEPT_EDGE",EDGE,{"disambiguationData":[OSD([sQuery(id+"F0.wireOp",EDGE,"E1.0"),sQuery(id+"F0.wireOp",EDGE,"E1.1"),sQuery(id+"F24.wireOp",EDGE,"E66.top"),sQuery(id+"F24.wireOp",EDGE,"E66.right")])]})});
            var Q6;
            Q6=makeQuery(id+"F25.boolean.opBoolean","COPY",EDGE,{"derivedFrom":makeQuery(id+"F25.opExtrude","SWEPT_EDGE",EDGE,{"disambiguationData":[OSD([sQuery(id+"F0.wireOp",EDGE,"E1.0"),sQuery(id+"F0.wireOp",EDGE,"E1.5"),sQuery(id+"F24.wireOp",EDGE,"E66.top"),sQuery(id+"F24.wireOp",EDGE,"E66.left")])]})});
            var Q7;
            Q7=makeQuery(id+"F25.boolean.opBoolean","COPY",EDGE,{"derivedFrom":makeQuery(id+"F25.opExtrude","SWEPT_EDGE",EDGE,{"disambiguationData":[OSD([sQuery(id+"F0.wireOp",EDGE,"E1.0"),sQuery(id+"F0.wireOp",EDGE,"E1.5"),sQuery(id+"F24.wireOp",EDGE,"E66.bottom"),sQuery(id+"F24.wireOp",EDGE,"E66.left")])]})});
            var Q8;
            Q8=makeQuery(id+"F23.boolean.opBoolean","COPY",EDGE,{"derivedFrom":makeQuery(id+"F23.opExtrude","SWEPT_EDGE",EDGE,{"disambiguationData":[OSD([sQuery(id+"F22.wireOp",EDGE,"E64.top"),sQuery(id+"F22.wireOp",EDGE,"E64.right")])]})});
            var Q9;
            Q9=makeQuery(id+"F23.boolean.opBoolean","COPY",EDGE,{"derivedFrom":makeQuery(id+"F23.opExtrude","SWEPT_EDGE",EDGE,{"disambiguationData":[OSD([sQuery(id+"F22.wireOp",EDGE,"E64.top"),sQuery(id+"F22.wireOp",EDGE,"E64.left")])]})});
            var Q10;
            Q10=makeQuery(id+"F23.boolean.opBoolean","COPY",EDGE,{"derivedFrom":makeQuery(id+"F23.opExtrude","SWEPT_EDGE",EDGE,{"disambiguationData":[OSD([sQuery(id+"F22.wireOp",EDGE,"E64.bottom"),sQuery(id+"F22.wireOp",EDGE,"E64.left")])]})});
            var Q11;
            Q11=makeQuery(id+"F23.boolean.opBoolean","COPY",EDGE,{"derivedFrom":makeQuery(id+"F23.opExtrude","SWEPT_EDGE",EDGE,{"disambiguationData":[OSD([sQuery(id+"F22.wireOp",EDGE,"E64.bottom"),sQuery(id+"F22.wireOp",EDGE,"E64.right")])]})});
            fillet(context, id + "F28", {"entities" : qUnion([Q0, Q1, Q2, Q3, Q4, Q5, Q6, Q7, Q8, Q9, Q10, Q11]), "radius" : 5 * mm, "tangentPropagation" : true, "allowEdgeOverflow" : false});
        }
        {
            var Q0;
            {var subQ3=sQuery(id+"F14.wireOp",EDGE,"E48");var subQ4=sQuery(id+"F14.wireOp",EDGE,"E46.0");var subQ5=sQuery(id+"F14.wireOp",EDGE,"E45.0");Q0=makeQuery(id+"F23.boolean.opBoolean","SPLIT",FACE,{"disambiguationData":[TD([makeQuery(id+"F13.opExtrude","SWEPT_FACE",FACE,{"disambiguationData":[OSD([sQuery(id+"F12.wireOp",EDGE,"E43.bottom")])]})])],"derivedFrom":makeQuery(id+"F15.boolean.opBoolean","MERGE",FACE,{"derivedFrom":[makeQuery(id+"F5.boolean.opBoolean","MERGE",FACE,{"derivedFrom":[makeQuery(id+"F1.opExtrude","SWEPT_FACE",FACE,{"disambiguationData":[OSD([sQuery(id+"F0.wireOp",EDGE,"E1.0")])]}),makeQuery(id+"F5.opExtrude","CAP_FACE",FACE,{"disambiguationData":[OSD([sQuery(id+"F4.wireOp",EDGE,"E7.0"),sQuery(id+"F4.wireOp",EDGE,"E8")])],"isStart":true})]}),makeQuery(id+"F15.opExtrude","CAP_FACE",FACE,{"disambiguationData":[OSD([subQ5,subQ4,sQuery(id+"F14.wireOp",EDGE,"E47.0"),subQ3])],"isStart":true})]})});}
            var sketch = newSketch(context, id + "F29", { "sketchPlane" : qUnion([Q0])});
            skLineSegment(sketch, "E71", {"start": v(19, -19) * mm, "end": v(-16.6, -19) * mm, "construction": true});
            skLineSegment(sketch, "E72.bottom", {"start": v(12.5, -6.5) * mm, "end": v(-12.5, -6.5) * mm, "construction": true});
            skLineSegment(sketch, "E72.top", {"start": v(12.5, -31.5) * mm, "end": v(-12.5, -31.5) * mm, "construction": true});
            skLineSegment(sketch, "E72.left", {"start": v(12.5, -6.5) * mm, "end": v(12.5, -31.5) * mm, "construction": true});
            skLineSegment(sketch, "E72.right", {"start": v(-12.5, -6.5) * mm, "end": v(-12.5, -31.5) * mm, "construction": true});
            skPoint(sketch, "E73", {"position": v(12.5, -19) * mm});
            skPoint(sketch, "E74", {"position": v(0, -31.5) * mm});
            skCircle(sketch, "E75", {"center": v(12.5, -6.5) * mm, "radius": 1.75 * mm});
            skCircle(sketch, "E76", {"center": v(-12.5, -6.5) * mm, "radius": 1.75 * mm});
            skCircle(sketch, "E77", {"center": v(-12.5, -31.5) * mm, "radius": 1.75 * mm});
            skCircle(sketch, "E78", {"center": v(12.5, -31.5) * mm, "radius": 1.75 * mm});
            skCircle(sketch, "E79", {"center": v(-12.5, -6.5) * mm, "radius": 3.5 * mm});
            skCircle(sketch, "E80", {"center": v(12.5, -6.5) * mm, "radius": 3.5 * mm});
            skCircle(sketch, "E81", {"center": v(12.5, -31.5) * mm, "radius": 3.5 * mm});
            skCircle(sketch, "E82", {"center": v(-12.5, -31.5) * mm, "radius": 3.5 * mm});
            skPoint(sketch, "E83", {"position": v(0, -38) * mm});
            skSolve(sketch);
        }
        {
            var Q0;
            Q0=makeQuery(id+"F29.imprint","IMPRINT",FACE,{"disambiguationData":[TD([[makeQuery(id+"F29.imprint","IMPRINT",EDGE,{"derivedFrom":sQuery(id+"F29.wireOp",EDGE,"E77")}),1.0]])]});
            var Q1;
            Q1=makeQuery(id+"F29.imprint","IMPRINT",FACE,{"disambiguationData":[TD([[makeQuery(id+"F29.imprint","IMPRINT",EDGE,{"derivedFrom":sQuery(id+"F29.wireOp",EDGE,"E76")}),1.0]])]});
            var Q2;
            Q2=makeQuery(id+"F29.imprint","IMPRINT",FACE,{"disambiguationData":[TD([[makeQuery(id+"F29.imprint","IMPRINT",EDGE,{"derivedFrom":sQuery(id+"F29.wireOp",EDGE,"E75")}),1.0]])]});
            var Q3;
            Q3=makeQuery(id+"F29.imprint","IMPRINT",FACE,{"disambiguationData":[TD([[makeQuery(id+"F29.imprint","IMPRINT",EDGE,{"derivedFrom":sQuery(id+"F29.wireOp",EDGE,"E78")}),1.0]])]});
            extrude(context, id + "F30", {"entities" : qUnion([Q0, Q1, Q2, Q3]), "operationType" : NewBodyOperationType.REMOVE, "endBound" : BoundingType.THROUGH_ALL, "oppositeDirection" : true, "depth" : 25 * mm, "offsetDistance" : 25 * mm});
        }
        {
            var Q0;
            {var subQ3=sQuery(id+"F14.wireOp",EDGE,"E48");var subQ4=sQuery(id+"F14.wireOp",EDGE,"E46.0");var subQ5=sQuery(id+"F14.wireOp",EDGE,"E45.0");Q0=makeQuery(id+"F23.boolean.opBoolean","SPLIT",FACE,{"disambiguationData":[TD([makeQuery(id+"F13.opExtrude","SWEPT_FACE",FACE,{"disambiguationData":[OSD([sQuery(id+"F12.wireOp",EDGE,"E43.bottom")])]})])],"derivedFrom":makeQuery(id+"F15.boolean.opBoolean","MERGE",FACE,{"derivedFrom":[makeQuery(id+"F5.boolean.opBoolean","MERGE",FACE,{"derivedFrom":[makeQuery(id+"F1.opExtrude","SWEPT_FACE",FACE,{"disambiguationData":[OSD([sQuery(id+"F0.wireOp",EDGE,"E1.0")])]}),makeQuery(id+"F5.opExtrude","CAP_FACE",FACE,{"disambiguationData":[OSD([sQuery(id+"F4.wireOp",EDGE,"E7.0"),sQuery(id+"F4.wireOp",EDGE,"E8")])],"isStart":true})]}),makeQuery(id+"F15.opExtrude","CAP_FACE",FACE,{"disambiguationData":[OSD([subQ5,subQ4,sQuery(id+"F14.wireOp",EDGE,"E47.0"),subQ3])],"isStart":true})]})});}
            var sketch = newSketch(context, id + "F31", { "sketchPlane" : qUnion([Q0])});
            skCircle(sketch, "E84.0", {"center": v(-12.5, -31.5) * mm, "radius": 1.75 * mm});
            skCircle(sketch, "E85.0", {"center": v(-12.5, -6.5) * mm, "radius": 1.75 * mm});
            skCircle(sketch, "E86.0", {"center": v(12.5, -6.5) * mm, "radius": 1.75 * mm});
            skCircle(sketch, "E87.0", {"center": v(12.5, -31.5) * mm, "radius": 1.75 * mm});
            skCircle(sketch, "E88", {"center": v(-12.5, -6.5) * mm, "radius": 3.5 * mm});
            skCircle(sketch, "E89", {"center": v(12.5, -6.5) * mm, "radius": 3.5 * mm});
            skCircle(sketch, "E90", {"center": v(12.5, -31.5) * mm, "radius": 3.5 * mm});
            skCircle(sketch, "E91", {"center": v(-12.5, -31.5) * mm, "radius": 3.5 * mm});
            skSolve(sketch);
        }
        {
            var Q0;
            Q0=makeQuery(id+"F31.imprint","IMPRINT",FACE,{"disambiguationData":[TD([[makeQuery(id+"F31.imprint","IMPRINT",EDGE,{"derivedFrom":sQuery(id+"F31.wireOp",EDGE,"E84.0")}),-1.0]])]});
            var Q1;
            Q1=makeQuery(id+"F31.imprint","IMPRINT",FACE,{"disambiguationData":[TD([[makeQuery(id+"F31.imprint","IMPRINT",EDGE,{"derivedFrom":sQuery(id+"F31.wireOp",EDGE,"E87.0")}),-1.0]])]});
            var Q2;
            Q2=makeQuery(id+"F31.imprint","IMPRINT",FACE,{"disambiguationData":[TD([[makeQuery(id+"F31.imprint","IMPRINT",EDGE,{"derivedFrom":sQuery(id+"F31.wireOp",EDGE,"E86.0")}),-1.0]])]});
            var Q3;
            Q3=makeQuery(id+"F31.imprint","IMPRINT",FACE,{"disambiguationData":[TD([[makeQuery(id+"F31.imprint","IMPRINT",EDGE,{"derivedFrom":sQuery(id+"F31.wireOp",EDGE,"E85.0")}),-1.0]])]});
            var Q4;
            {var subQ2=sQuery(id+"F12.wireOp",EDGE,"E43.right");var subQ3=sQuery(id+"F12.wireOp",EDGE,"E43.left");var subQ6=sQuery(id+"F12.wireOp",EDGE,"E43.top");var subQ7=sQuery(id+"F12.wireOp",EDGE,"E43.bottom");Q4=makeQuery(id+"F27.boolean.opBoolean","SPLIT",FACE,{"disambiguationData":[TD([makeQuery(id+"F13.opExtrude","SWEPT_FACE",FACE,{"disambiguationData":[OSD([subQ7])]})])],"derivedFrom":makeQuery(id+"F13.boolean.opBoolean","MERGE",FACE,{"derivedFrom":[makeQuery(id+"F3.boolean.opBoolean","MERGE",FACE,{"derivedFrom":[makeQuery(id+"F1.opExtrude","SWEPT_FACE",FACE,{"disambiguationData":[OSD([sQuery(id+"F0.wireOp",EDGE,"E1.3")])]}),makeQuery(id+"F3.opExtrude","CAP_FACE",FACE,{"disambiguationData":[OSD([sQuery(id+"F2.wireOp",EDGE,"E6")])],"isStart":true})]}),makeQuery(id+"F13.opExtrude","CAP_FACE",FACE,{"disambiguationData":[OSD([subQ7,subQ6,subQ3,subQ2])],"isStart":true})]})});}
            extrude(context, id + "F32", {"entities" : qUnion([Q0, Q1, Q2, Q3]), "operationType" : NewBodyOperationType.ADD, "endBound" : BoundingType.UP_TO_SURFACE, "oppositeDirection" : true, "depth" : 25 * mm, "endBoundEntityFace" : qUnion([Q4]), "offsetDistance" : 25 * mm});
        }
        {
            var Q0;
            Q0=makeQuery(id+"F27.boolean.opBoolean","COPY",FACE,{"derivedFrom":makeQuery(id+"F27.opExtrude","CAP_FACE",FACE,{"disambiguationData":[OSD([sQuery(id+"F26.wireOp",EDGE,"E67.0"),sQuery(id+"F26.wireOp",EDGE,"E68.0"),sQuery(id+"F26.wireOp",EDGE,"E69.0"),sQuery(id+"F26.wireOp",EDGE,"E70.0")])],"isStart":false})});
            var sketch = newSketch(context, id + "F33", { "sketchPlane" : qUnion([Q0])});
            skLineSegment(sketch, "E92.0.0", {"start": v(-1, -188.85) * mm, "end": v(-1, -208.85) * mm});
            skLineSegment(sketch, "E92.0.1", {"start": v(-1, -208.85) * mm, "end": v(1, -208.85) * mm});
            skLineSegment(sketch, "E92.0.2", {"start": v(1, -208.85) * mm, "end": v(1, -188.85) * mm});
            skLineSegment(sketch, "E92.0.3", {"start": v(1, -188.85) * mm, "end": v(-1, -188.85) * mm});
            skSolve(sketch);
        }
        {
            var Q0;
            Q0 = qSketchRegion(id + "F33", true);
            var Q1;
            {var subQ2=sQuery(id+"F12.wireOp",EDGE,"E43.right");var subQ3=sQuery(id+"F12.wireOp",EDGE,"E43.left");var subQ6=sQuery(id+"F12.wireOp",EDGE,"E43.top");var subQ7=sQuery(id+"F12.wireOp",EDGE,"E43.bottom");Q1=makeQuery(id+"F27.boolean.opBoolean","SPLIT",FACE,{"disambiguationData":[TD([makeQuery(id+"F13.opExtrude","SWEPT_FACE",FACE,{"disambiguationData":[OSD([subQ7])]})])],"derivedFrom":makeQuery(id+"F13.boolean.opBoolean","MERGE",FACE,{"derivedFrom":[makeQuery(id+"F3.boolean.opBoolean","MERGE",FACE,{"derivedFrom":[makeQuery(id+"F1.opExtrude","SWEPT_FACE",FACE,{"disambiguationData":[OSD([sQuery(id+"F0.wireOp",EDGE,"E1.3")])]}),makeQuery(id+"F3.opExtrude","CAP_FACE",FACE,{"disambiguationData":[OSD([sQuery(id+"F2.wireOp",EDGE,"E6")])],"isStart":true})]}),makeQuery(id+"F13.opExtrude","CAP_FACE",FACE,{"disambiguationData":[OSD([subQ7,subQ6,subQ3,subQ2])],"isStart":true})]})});}
            extrude(context, id + "F34", {"entities" : qUnion([Q0]), "operationType" : NewBodyOperationType.ADD, "endBound" : BoundingType.UP_TO_SURFACE, "depth" : 25 * mm, "endBoundEntityFace" : qUnion([Q1]), "offsetDistance" : 25 * mm});
        }
    });
